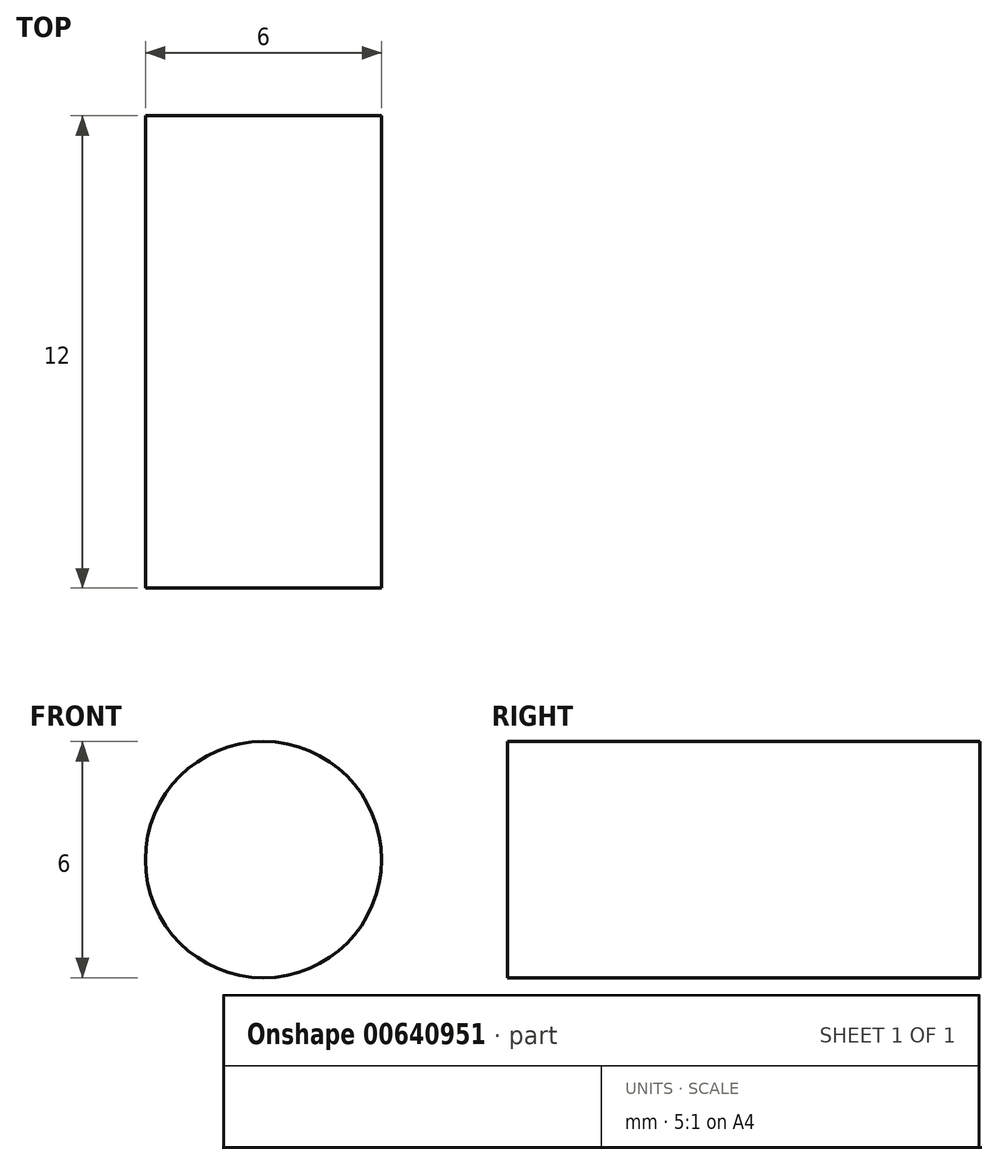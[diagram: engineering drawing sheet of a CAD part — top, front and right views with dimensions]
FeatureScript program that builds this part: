
annotation { "Feature Type Name" : "Feature", "Feature Type Description" : "" }
export const myFeature = defineFeature(function(context is Context, id is Id, definition is map)
    precondition{}
    {
        {
            var Q0;
            Q0=qCreatedBy(makeId("Front.planeOp"),FACE);
            var sketch = newSketch(context, id + "F0", { "sketchPlane" : qUnion([Q0])});
            skLineSegment(sketch, "E0.bottom", {"start": v(-49.04, -16.35) * mm, "end": v(50.95, -16.35) * mm});
            skLineSegment(sketch, "E0.top", {"start": v(-49.04, 18.5) * mm, "end": v(50.95, 18.5) * mm});
            skLineSegment(sketch, "E0.left", {"start": v(-49.04, -16.35) * mm, "end": v(-49.04, 18.5) * mm});
            skLineSegment(sketch, "E0.right", {"start": v(50.95, -16.35) * mm, "end": v(50.95, 18.5) * mm});
            skSolve(sketch);
        }
        {
            var Q0;
            Q0=makeQuery(id+"F0.imprint","IMPRINT",FACE,{"disambiguationData":[TD([[makeQuery(id+"F0.imprint","IMPRINT",EDGE,{"derivedFrom":sQuery(id+"F0.wireOp",EDGE,"E0.bottom")}),1.0]])]});
            extrude(context, id + "F1", {"entities" : qUnion([Q0]), "depth" : 12 * mm, "offsetDistance" : 25 * mm});
        }
        {
            var Q0;
            Q0=makeQuery(id+"F1.opExtrude","CAP_FACE",FACE,{"disambiguationData":[OSD([sQuery(id+"F0.wireOp",EDGE,"E0.bottom"),sQuery(id+"F0.wireOp",EDGE,"E0.top"),sQuery(id+"F0.wireOp",EDGE,"E0.left"),sQuery(id+"F0.wireOp",EDGE,"E0.right")])],"isStart":true});
            var sketch = newSketch(context, id + "F2", { "sketchPlane" : qUnion([Q0])});
            skCircle(sketch, "E1", {"center": v(-28.04, 0) * mm, "radius": 3 * mm});
            skCircle(sketch, "E2.MirrorC", {"center": v(28.04, 0) * mm, "radius": 3 * mm});
            skSolve(sketch);
        }
        {
            var Q0;
            Q0=makeQuery(id+"F2.imprint","IMPRINT",FACE,{"disambiguationData":[TD([[makeQuery(id+"F2.imprint","IMPRINT",EDGE,{"derivedFrom":sQuery(id+"F2.wireOp",EDGE,"E1")}),1.0]])]});
            var Q1;
            Q1=makeQuery(id+"F2.imprint","IMPRINT",FACE,{"disambiguationData":[TD([[makeQuery(id+"F2.imprint","IMPRINT",EDGE,{"derivedFrom":sQuery(id+"F2.wireOp",EDGE,"E2.MirrorC")}),-1.0]])]});
            extrude(context, id + "F3", {"entities" : qUnion([Q0, Q1]), "operationType" : NewBodyOperationType.REMOVE, "oppositeDirection" : true, "depth" : 75 * mm, "offsetDistance" : 25 * mm});
        }
    });
